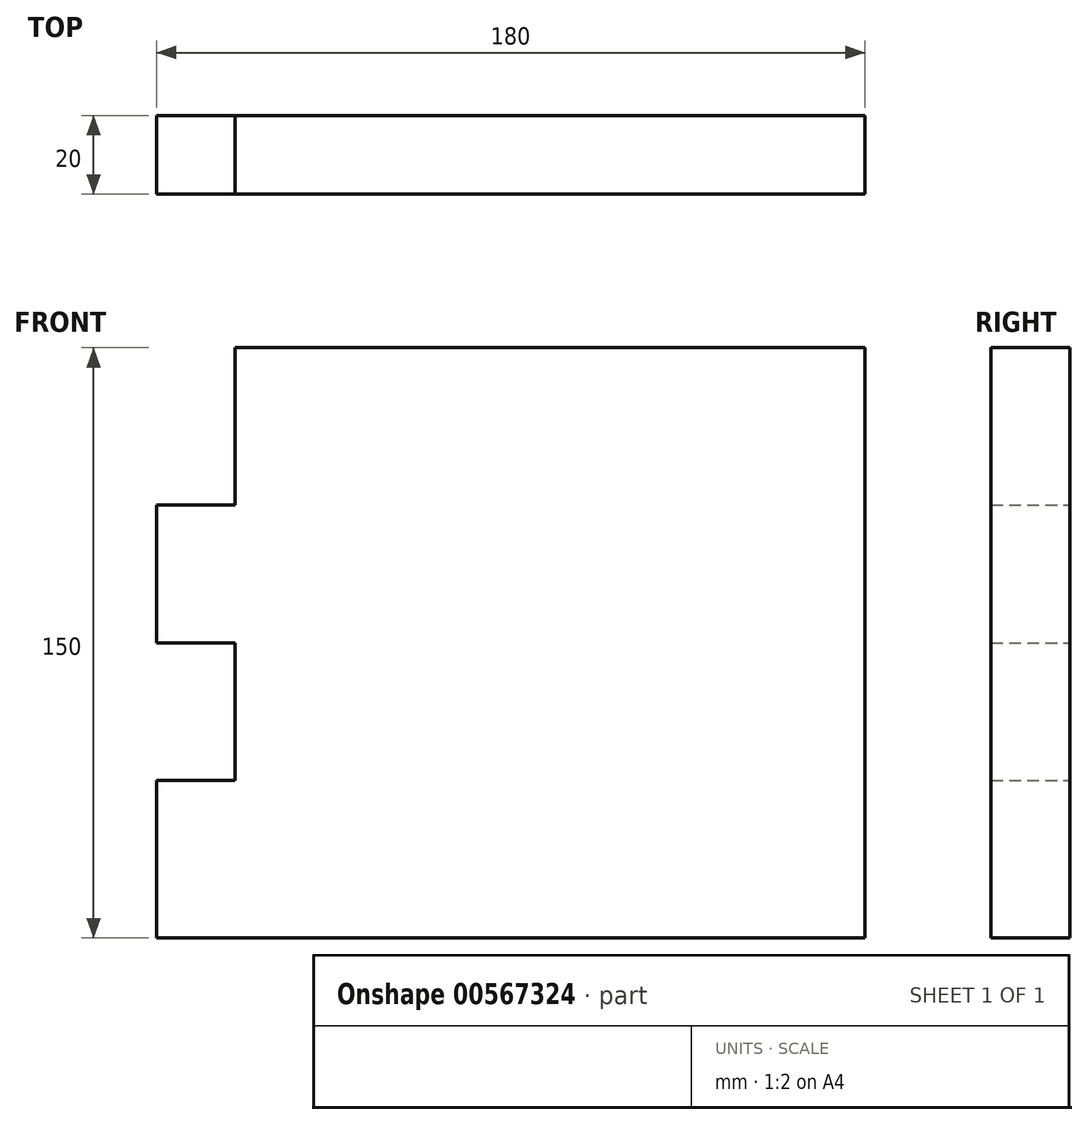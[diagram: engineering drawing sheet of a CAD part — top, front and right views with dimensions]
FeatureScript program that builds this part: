
annotation { "Feature Type Name" : "Feature", "Feature Type Description" : "" }
export const myFeature = defineFeature(function(context is Context, id is Id, definition is map)
    precondition{}
    {
        {
            var Q0;
            Q0=qCreatedBy(makeId("Front.planeOp"),FACE);
            var sketch = newSketch(context, id + "F0", { "sketchPlane" : qUnion([Q0])});
            skLineSegment(sketch, "E0.bottom", {"start": v(-71, 73.58) * mm, "end": v(89, 73.58) * mm});
            skLineSegment(sketch, "E0.top", {"start": v(-91, -76.42) * mm, "end": v(89, -76.42) * mm});
            skLineSegment(sketch, "E0.left", {"start": v(-91, 33.58) * mm, "end": v(-91, -1.42) * mm});
            skLineSegment(sketch, "E0.right", {"start": v(89, 73.58) * mm, "end": v(89, -76.42) * mm});
            skLineSegment(sketch, "E1", {"start": v(-71, 73.58) * mm, "end": v(-71, -76.42) * mm});
            skLineSegment(sketch, "E2", {"start": v(-71, -1.42) * mm, "end": v(-91, -1.42) * mm});
            skLineSegment(sketch, "E3", {"start": v(-91, 33.58) * mm, "end": v(-71, 33.58) * mm});
            skLineSegment(sketch, "E4", {"start": v(-91, -36.42) * mm, "end": v(-71, -36.42) * mm});
            skPoint(sketch, "E5.orphan", {"position": v(-91, 73.58) * mm});
            skLineSegment(sketch, "E6.trimOffspring", {"start": v(-91, -36.42) * mm, "end": v(-91, -76.42) * mm});
            skSolve(sketch);
        }
        {
            var Q0;
            Q0 = qSketchRegion(id + "F0", true);
            extrude(context, id + "F1", {"entities" : qUnion([Q0]), "depth" : 20 * mm, "offsetDistance" : 25.4 * mm});
        }
    });
